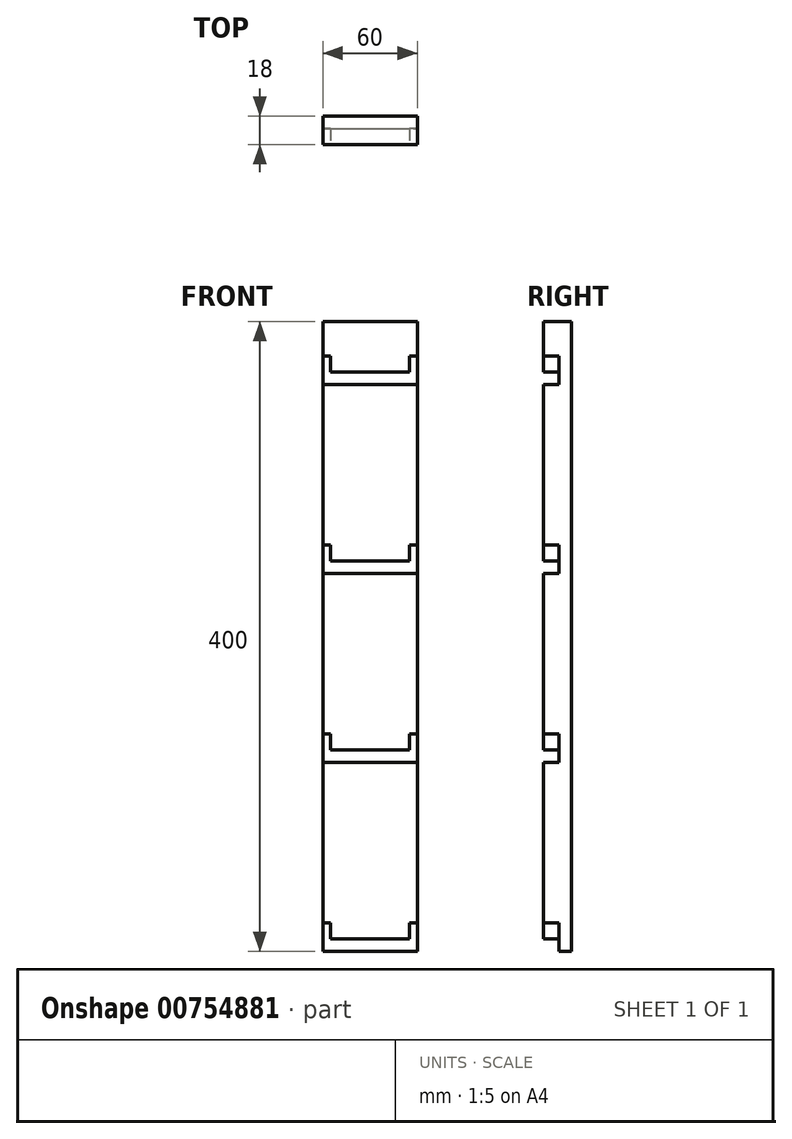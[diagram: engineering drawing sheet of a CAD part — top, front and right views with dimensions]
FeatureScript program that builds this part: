
annotation { "Feature Type Name" : "Feature", "Feature Type Description" : "" }
export const myFeature = defineFeature(function(context is Context, id is Id, definition is map)
    precondition{}
    {
        {
            var Q0;
            Q0=qCreatedBy(makeId("Top.planeOp"),FACE);
            var sketch = newSketch(context, id + "F0", { "sketchPlane" : qUnion([Q0])});
            skLineSegment(sketch, "E0.bottom", {"start": v(-102.74, 12.86) * mm, "end": v(-42.74, 12.86) * mm});
            skLineSegment(sketch, "E0.top", {"start": v(-102.74, -5.14) * mm, "end": v(-42.74, -5.14) * mm});
            skLineSegment(sketch, "E0.left", {"start": v(-102.74, 12.86) * mm, "end": v(-102.74, -5.14) * mm});
            skLineSegment(sketch, "E0.right", {"start": v(-42.74, 12.86) * mm, "end": v(-42.74, -5.14) * mm});
            skSolve(sketch);
        }
        {
            var Q0;
            Q0 = qSketchRegion(id + "F0", true);
            extrude(context, id + "F1", {"entities" : qUnion([Q0]), "depth" : 400 * mm, "offsetDistance" : 25 * mm});
        }
        {
            var Q0;
            Q0=makeQuery(id+"F1.opExtrude","SWEPT_FACE",FACE,{"disambiguationData":[OSD([sQuery(id+"F0.wireOp",EDGE,"E0.top")])]});
            var sketch = newSketch(context, id + "F2", { "sketchPlane" : qUnion([Q0])});
            skLineSegment(sketch, "E1.bottom", {"start": v(-42.74, 0) * mm, "end": v(-102.74, 0) * mm});
            skLineSegment(sketch, "E1.top", {"start": v(-42.74, 18) * mm, "end": v(-47.74, 18) * mm});
            skLineSegment(sketch, "E1.left", {"start": v(-42.74, 0) * mm, "end": v(-42.74, 18) * mm});
            skLineSegment(sketch, "E1.right", {"start": v(-102.74, 0) * mm, "end": v(-102.74, 18) * mm});
            skLineSegment(sketch, "E2.top", {"start": v(-97.74, 8) * mm, "end": v(-47.74, 8) * mm});
            skLineSegment(sketch, "E2.left", {"start": v(-97.74, 18) * mm, "end": v(-97.74, 8) * mm});
            skLineSegment(sketch, "E2.right", {"start": v(-47.74, 18) * mm, "end": v(-47.74, 8) * mm});
            skLineSegment(sketch, "E3.trimOffspring", {"start": v(-97.74, 18) * mm, "end": v(-102.74, 18) * mm});
            skLineSegment(sketch, "E4.0.1.0", {"start": v(-102.74, 120) * mm, "end": v(-102.74, 138) * mm});
            skLineSegment(sketch, "E4.0.1.1", {"start": v(-97.74, 128) * mm, "end": v(-47.74, 128) * mm});
            skLineSegment(sketch, "E4.0.1.2", {"start": v(-97.74, 138) * mm, "end": v(-97.74, 128) * mm});
            skLineSegment(sketch, "E4.0.1.3", {"start": v(-47.74, 138) * mm, "end": v(-47.74, 128) * mm});
            skLineSegment(sketch, "E4.0.1.4", {"start": v(-97.74, 138) * mm, "end": v(-102.74, 138) * mm});
            skLineSegment(sketch, "E4.0.1.5", {"start": v(-42.74, 120) * mm, "end": v(-42.74, 138) * mm});
            skLineSegment(sketch, "E4.0.1.6", {"start": v(-42.74, 138) * mm, "end": v(-47.74, 138) * mm});
            skLineSegment(sketch, "E4.0.1.7", {"start": v(-42.74, 120) * mm, "end": v(-102.74, 120) * mm});
            skLineSegment(sketch, "E4.0.2.0", {"start": v(-102.74, 240) * mm, "end": v(-102.74, 258) * mm});
            skLineSegment(sketch, "E4.0.2.1", {"start": v(-97.74, 248) * mm, "end": v(-47.74, 248) * mm});
            skLineSegment(sketch, "E4.0.2.2", {"start": v(-97.74, 258) * mm, "end": v(-97.74, 248) * mm});
            skLineSegment(sketch, "E4.0.2.3", {"start": v(-47.74, 258) * mm, "end": v(-47.74, 248) * mm});
            skLineSegment(sketch, "E4.0.2.4", {"start": v(-97.74, 258) * mm, "end": v(-102.74, 258) * mm});
            skLineSegment(sketch, "E4.0.2.5", {"start": v(-42.74, 240) * mm, "end": v(-42.74, 258) * mm});
            skLineSegment(sketch, "E4.0.2.6", {"start": v(-42.74, 258) * mm, "end": v(-47.74, 258) * mm});
            skLineSegment(sketch, "E4.0.2.7", {"start": v(-42.74, 240) * mm, "end": v(-102.74, 240) * mm});
            skLineSegment(sketch, "E4.0.3.0", {"start": v(-102.74, 360) * mm, "end": v(-102.74, 378) * mm});
            skLineSegment(sketch, "E4.0.3.1", {"start": v(-97.74, 368) * mm, "end": v(-47.74, 368) * mm});
            skLineSegment(sketch, "E4.0.3.2", {"start": v(-97.74, 378) * mm, "end": v(-97.74, 368) * mm});
            skLineSegment(sketch, "E4.0.3.3", {"start": v(-47.74, 378) * mm, "end": v(-47.74, 368) * mm});
            skLineSegment(sketch, "E4.0.3.4", {"start": v(-97.74, 378) * mm, "end": v(-102.74, 378) * mm});
            skLineSegment(sketch, "E4.0.3.5", {"start": v(-42.74, 360) * mm, "end": v(-42.74, 378) * mm});
            skLineSegment(sketch, "E4.0.3.6", {"start": v(-42.74, 378) * mm, "end": v(-47.74, 378) * mm});
            skLineSegment(sketch, "E4.0.3.7", {"start": v(-42.74, 360) * mm, "end": v(-102.74, 360) * mm});
            skLineSegment(sketch, "E4.direction1", {"start": v(-102.74, 0) * mm, "end": v(-77.74, 0) * mm, "construction": true});
            skLineSegment(sketch, "E4.direction2", {"start": v(-102.74, 0) * mm, "end": v(-102.74, 120) * mm, "construction": true});
            skSolve(sketch);
        }
        {
            var Q0;
            Q0 = qSketchRegion(id + "F2", true);
            extrude(context, id + "F3", {"entities" : qUnion([Q0]), "operationType" : NewBodyOperationType.REMOVE, "oppositeDirection" : true, "depth" : 10 * mm, "offsetDistance" : 25 * mm});
        }
    });
